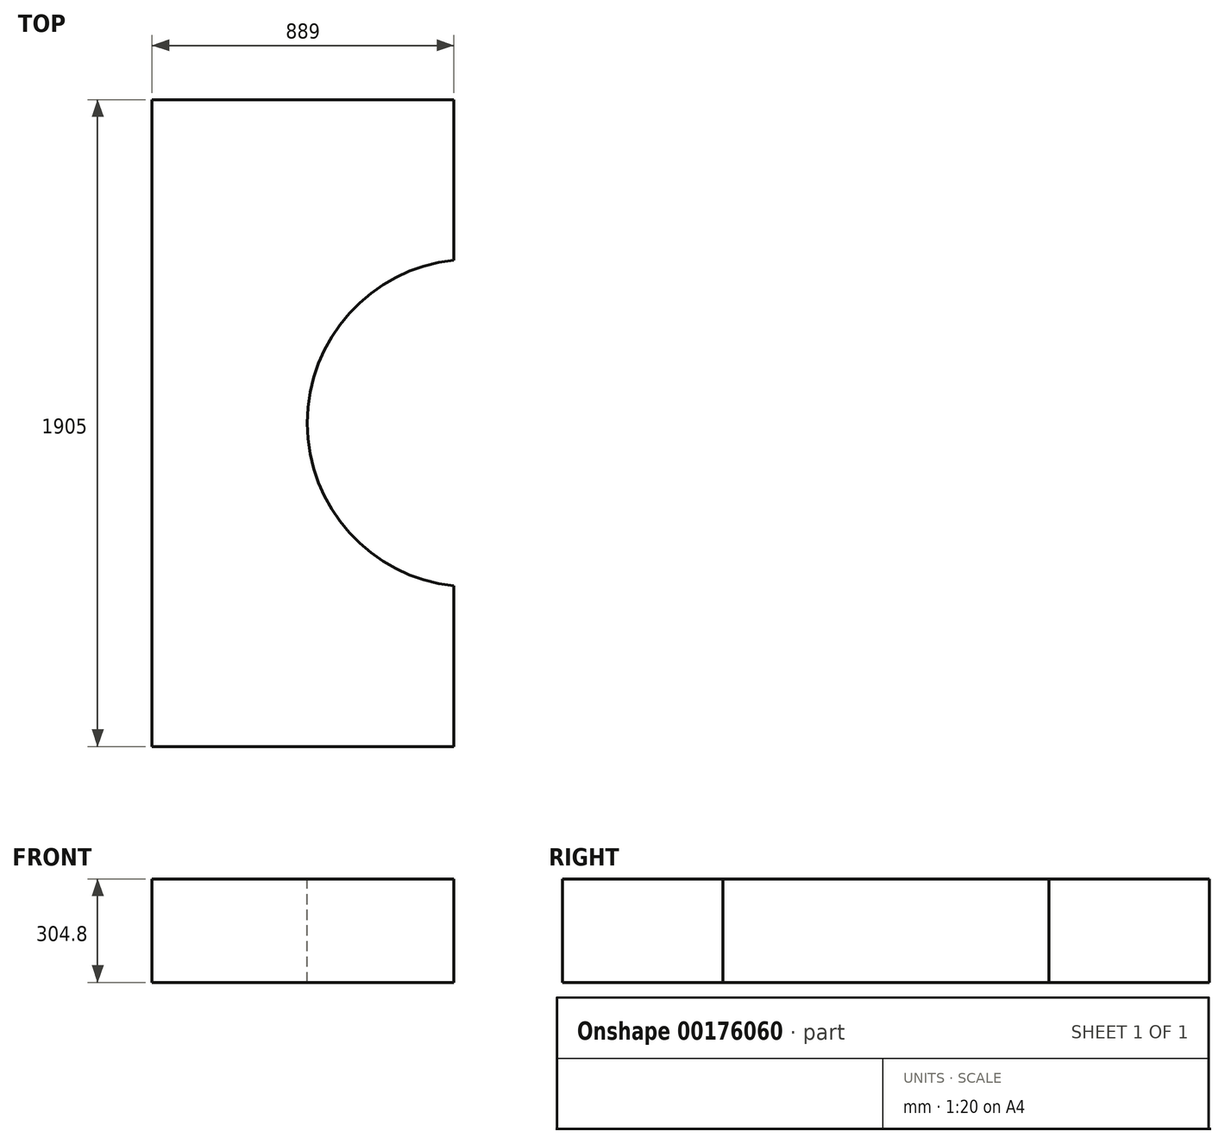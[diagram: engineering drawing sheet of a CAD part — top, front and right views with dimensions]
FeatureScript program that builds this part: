
annotation { "Feature Type Name" : "Feature", "Feature Type Description" : "" }
export const myFeature = defineFeature(function(context is Context, id is Id, definition is map)
    precondition{}
    {
        {
            var Q0;
            Q0=qCreatedBy(makeId("Front.planeOp"),FACE);
            var sketch = newSketch(context, id + "F0", { "sketchPlane" : qUnion([Q0])});
            skLineSegment(sketch, "E0.bottom", {"start": v(444.5, 152.4) * mm, "end": v(-444.5, 152.4) * mm});
            skLineSegment(sketch, "E0.top", {"start": v(444.5, -152.4) * mm, "end": v(-444.5, -152.4) * mm});
            skLineSegment(sketch, "E0.left", {"start": v(444.5, 152.4) * mm, "end": v(444.5, -152.4) * mm});
            skLineSegment(sketch, "E0.right", {"start": v(-444.5, 152.4) * mm, "end": v(-444.5, -152.4) * mm});
            skPoint(sketch, "E0.middle", {"position": v(0, 0) * mm});
            skSolve(sketch);
        }
        {
            var Q0;
            Q0=makeQuery(id+"F0.imprint","IMPRINT",FACE,{"disambiguationData":[TD([[makeQuery(id+"F0.imprint","IMPRINT",EDGE,{"derivedFrom":sQuery(id+"F0.wireOp",EDGE,"E0.bottom")}),1.0]])]});
            extrude(context, id + "F1", {"entities" : qUnion([Q0]), "endBound" : BoundingType.SYMMETRIC, "depth" : 1905 * mm});
        }
        {
            var Q0;
            Q0=makeQuery(id+"F1.opExtrude","SWEPT_FACE",FACE,{"disambiguationData":[OSD([sQuery(id+"F0.wireOp",EDGE,"E0.bottom")])]});
            var sketch = newSketch(context, id + "F2", { "sketchPlane" : qUnion([Q0])});
            skLineSegment(sketch, "E1", {"start": v(-444.5, 0) * mm, "end": v(883.89, 0) * mm});
            skPoint(sketch, "E1.endSnap0", {"position": v(444.5, 0) * mm});
            skLineSegment(sketch, "E2", {"start": v(444.5, -952.5) * mm, "end": v(495.3, -952.5) * mm});
            skLineSegment(sketch, "E3", {"start": v(495.3, -952.5) * mm, "end": v(495.3, 0) * mm});
            skArc(sketch, "E4", {"start": v(444.5, -479.92) * mm, "mid": v(12.7, 0) * mm, "end": v(444.5, 479.92) * mm});
            skSolve(sketch);
        }
        {
            var Q0;
            {var subQ0=sQuery(id+"F2.wireOp",EDGE,"E4");var subQ1=sQuery(id+"F2.wireOp",EDGE,"E1");var subQ2=makeQuery(id+"F2.imprint","INTERSECT",VERTEX,{"derivedFrom":[subQ1,subQ0]});Q0=makeQuery(id+"F2.imprint","IMPRINT",FACE,{"disambiguationData":[TD([[makeQuery(id+"F2.imprint","IMPRINT",EDGE,{"disambiguationData":[TD([[subQ2,-1.0]])],"derivedFrom":subQ1}),1.0]])]});}
            var Q1;
            {var subQ0=sQuery(id+"F2.wireOp",EDGE,"E4");var subQ1=sQuery(id+"F2.wireOp",EDGE,"E1");var subQ2=makeQuery(id+"F2.imprint","INTERSECT",VERTEX,{"derivedFrom":[subQ1,subQ0]});Q1=makeQuery(id+"F2.imprint","IMPRINT",FACE,{"disambiguationData":[TD([[makeQuery(id+"F2.imprint","IMPRINT",EDGE,{"disambiguationData":[TD([[subQ2,-1.0]])],"derivedFrom":subQ1}),-1.0]])]});}
            extrude(context, id + "F3", {"entities" : qUnion([Q0, Q1]), "operationType" : NewBodyOperationType.REMOVE, "endBound" : BoundingType.UP_TO_NEXT, "oppositeDirection" : true, "depth" : 25.4 * mm});
        }
    });
